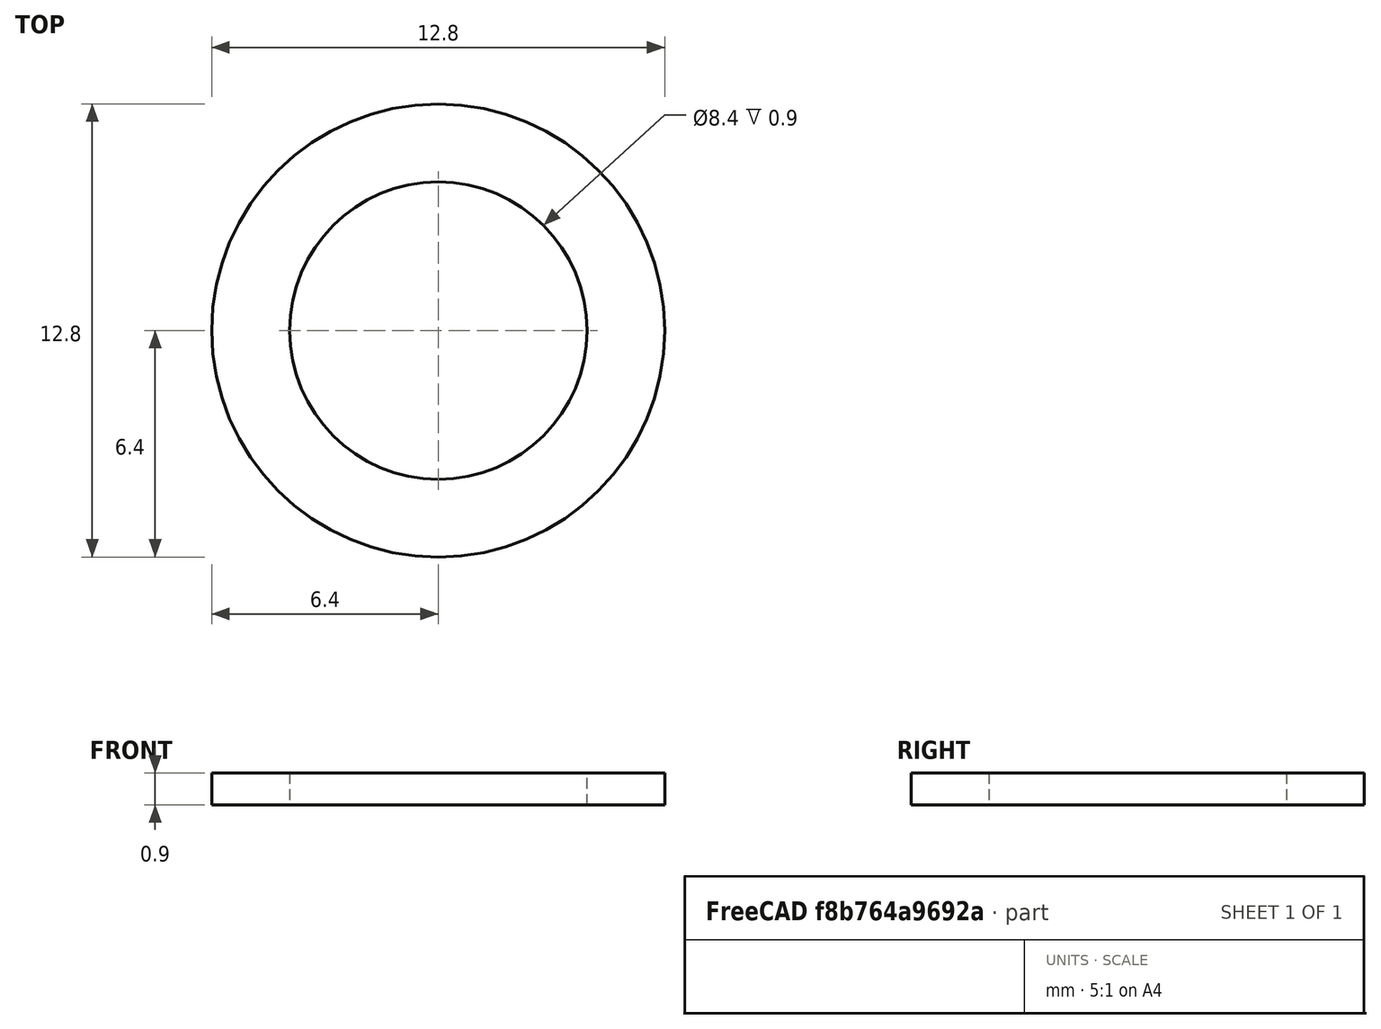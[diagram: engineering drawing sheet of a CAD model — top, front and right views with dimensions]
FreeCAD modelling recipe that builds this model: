
FCSTD DOCUMENT  (FreeCAD 0.18R16110 (Git))
Label: m8schnorrxs
License: All rights reserved
LicenseURL: http://en.wikipedia.org/wiki/All_rights_reserved
objects: Sketcher::SketchObject×1, PartDesign::Pad×1, PartDesign::Body×1
note: 4 computed .brp shape members not serialized (recipe doc carries the construction recipe); baked Part::Feature solids carry a one-line shape summary decoded from their .brp

FEATURE [Sketcher::SketchObject] Sketch
  MapMode = 5
  Support = -> [XY_Plane]
  sketch-geometry (2):
    g0: Circle CenterX=0 CenterY=0 CenterZ=0 NormalX=0 NormalY=0 NormalZ=1 AngleXU=0 Radius=6.4
    g1: Circle CenterX=0 CenterY=0 CenterZ=0 NormalX=0 NormalY=0 NormalZ=1 AngleXU=0 Radius=4.2
  constraints (4):
    c: Radius(g0) = 6.4
    c: Radius(g1) = 4.2
    c: Coincident(g1,g-1)
    c: Coincident(g0,g1)
FEATURE [PartDesign::Pad] Pad
  Length = 0.9
  Length2 = 100
  Profile = -> Sketch
  Type = 0
FEATURE [PartDesign::Body] Body
  Group = -> [Sketch,Pad]
  Origin = -> Origin
  Tip = -> Pad
